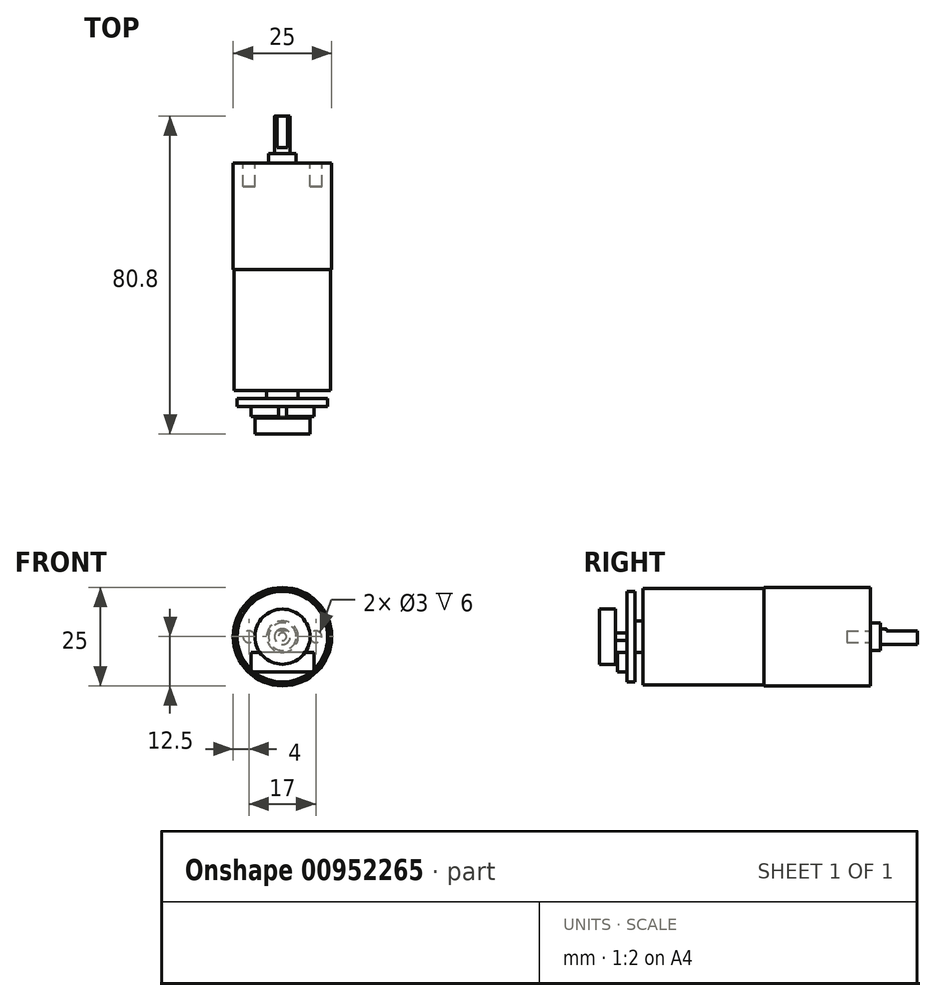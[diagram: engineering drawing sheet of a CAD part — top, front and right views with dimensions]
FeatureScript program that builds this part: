
annotation { "Feature Type Name" : "Feature", "Feature Type Description" : "" }
export const myFeature = defineFeature(function(context is Context, id is Id, definition is map)
    precondition{}
    {
        {
            var Q0;
            Q0=qCreatedBy(makeId("Front.planeOp"),FACE);
            var sketch = newSketch(context, id + "F0", { "sketchPlane" : qUnion([Q0])});
            skCircle(sketch, "E0", {"center": v(0, 0) * mm, "radius": 12.5 * mm});
            skSolve(sketch);
        }
        {
            var Q0;
            Q0 = qSketchRegion(id + "F0", true);
            extrude(context, id + "F1", {"entities" : qUnion([Q0]), "depth" : 27 * mm, "offsetDistance" : 25 * mm});
        }
        {
            var Q0;
            Q0=makeQuery(id+"F1.opExtrude","CAP_FACE",FACE,{"disambiguationData":[OSD([sQuery(id+"F0.wireOp",EDGE,"E0")])],"isStart":false});
            var sketch = newSketch(context, id + "F2", { "sketchPlane" : qUnion([Q0])});
            skCircle(sketch, "E1", {"center": v(0, 0) * mm, "radius": 12.25 * mm});
            skSolve(sketch);
        }
        {
            var Q0;
            Q0 = qSketchRegion(id + "F2", true);
            extrude(context, id + "F3", {"entities" : qUnion([Q0]), "operationType" : NewBodyOperationType.ADD, "depth" : 30.8 * mm, "offsetDistance" : 25 * mm});
        }
        {
            var Q0;
            Q0=makeQuery(id+"F1.opExtrude","CAP_FACE",FACE,{"disambiguationData":[OSD([sQuery(id+"F0.wireOp",EDGE,"E0")])],"isStart":true});
            var sketch = newSketch(context, id + "F4", { "sketchPlane" : qUnion([Q0])});
            skCircle(sketch, "E2", {"center": v(0, 0) * mm, "radius": 3.5 * mm});
            skSolve(sketch);
        }
        {
            var Q0;
            Q0 = qSketchRegion(id + "F4", true);
            extrude(context, id + "F5", {"entities" : qUnion([Q0]), "operationType" : NewBodyOperationType.ADD, "depth" : 2.5 * mm, "offsetDistance" : 25 * mm});
        }
        {
            var Q0;
            Q0=makeQuery(id+"F5.opExtrude","CAP_FACE",FACE,{"disambiguationData":[OSD([sQuery(id+"F4.wireOp",EDGE,"E2")])],"isStart":false});
            var sketch = newSketch(context, id + "F6", { "sketchPlane" : qUnion([Q0])});
            skCircle(sketch, "E3", {"center": v(0, 0) * mm, "radius": 2 * mm});
            skSolve(sketch);
        }
        {
            var Q0;
            Q0 = qSketchRegion(id + "F6", true);
            extrude(context, id + "F7", {"entities" : qUnion([Q0]), "operationType" : NewBodyOperationType.ADD, "depth" : 9.5 * mm, "offsetDistance" : 25 * mm});
        }
        {
            var Q0;
            Q0=makeQuery(id+"F7.opExtrude","CAP_FACE",FACE,{"disambiguationData":[OSD([sQuery(id+"F6.wireOp",EDGE,"E3")])],"isStart":false});
            var sketch = newSketch(context, id + "F8", { "sketchPlane" : qUnion([Q0])});
            skLineSegment(sketch, "E4", {"start": v(-1.32, 1.5) * mm, "end": v(1.32, 1.5) * mm});
            skArc(sketch, "E5", {"start": v(-1.32, 1.5) * mm, "mid": v(0, 2) * mm, "end": v(1.32, 1.5) * mm});
            skSolve(sketch);
        }
        {
            var Q0;
            Q0 = qSketchRegion(id + "F8", true);
            extrude(context, id + "F9", {"entities" : qUnion([Q0]), "operationType" : NewBodyOperationType.REMOVE, "oppositeDirection" : true, "depth" : 8 * mm, "offsetDistance" : 25 * mm});
        }
        {
            var Q0;
            Q0=makeQuery(id+"F1.opExtrude","CAP_FACE",FACE,{"disambiguationData":[OSD([sQuery(id+"F0.wireOp",EDGE,"E0")])],"isStart":true});
            var sketch = newSketch(context, id + "F10", { "sketchPlane" : qUnion([Q0])});
            skCircle(sketch, "E6", {"center": v(8.5, 0) * mm, "radius": 1.5 * mm});
            skCircle(sketch, "E7.MirrorC", {"center": v(-8.5, 0) * mm, "radius": 1.5 * mm});
            skSolve(sketch);
        }
        {
            var Q0;
            Q0 = qSketchRegion(id + "F10", true);
            extrude(context, id + "F11", {"entities" : qUnion([Q0]), "operationType" : NewBodyOperationType.REMOVE, "oppositeDirection" : true, "depth" : 6 * mm, "offsetDistance" : 25 * mm});
        }
        {
            var Q0;
            Q0=makeQuery(id+"F3.opExtrude","CAP_FACE",FACE,{"disambiguationData":[OSD([sQuery(id+"F2.wireOp",EDGE,"E1")])],"isStart":false});
            var sketch = newSketch(context, id + "F12", { "sketchPlane" : qUnion([Q0])});
            skCircle(sketch, "E8", {"center": v(0, 0) * mm, "radius": 4 * mm});
            skSolve(sketch);
        }
        {
            var Q0;
            Q0 = qSketchRegion(id + "F12", true);
            extrude(context, id + "F13", {"entities" : qUnion([Q0]), "operationType" : NewBodyOperationType.ADD, "depth" : 2 * mm, "offsetDistance" : 25 * mm});
        }
        {
            var Q0;
            Q0=makeQuery(id+"F13.opExtrude","CAP_FACE",FACE,{"disambiguationData":[OSD([sQuery(id+"F12.wireOp",EDGE,"E8")])],"isStart":false});
            var sketch = newSketch(context, id + "F14", { "sketchPlane" : qUnion([Q0])});
            skCircle(sketch, "E9", {"center": v(0, 0) * mm, "radius": 11.5 * mm});
            skSolve(sketch);
        }
        {
            var Q0;
            Q0 = qSketchRegion(id + "F14", true);
            extrude(context, id + "F15", {"entities" : qUnion([Q0]), "operationType" : NewBodyOperationType.ADD, "depth" : 2 * mm, "offsetDistance" : 25 * mm});
        }
        {
            var Q0;
            Q0=makeQuery(id+"F15.opExtrude","CAP_FACE",FACE,{"disambiguationData":[OSD([sQuery(id+"F14.wireOp",EDGE,"E9")])],"isStart":false});
            var sketch = newSketch(context, id + "F16", { "sketchPlane" : qUnion([Q0])});
            skCircle(sketch, "E10", {"center": v(0, 0) * mm, "radius": 1 * mm});
            skSolve(sketch);
        }
        {
            var Q0;
            Q0 = qSketchRegion(id + "F16", true);
            extrude(context, id + "F17", {"entities" : qUnion([Q0]), "operationType" : NewBodyOperationType.ADD, "depth" : (3.5 - 0.5) * mm, "offsetDistance" : 25 * mm});
        }
        {
            var Q0;
            Q0=makeQuery(id+"F17.opExtrude","CAP_FACE",FACE,{"disambiguationData":[OSD([sQuery(id+"F16.wireOp",EDGE,"E10")])],"isStart":false});
            var sketch = newSketch(context, id + "F18", { "sketchPlane" : qUnion([Q0])});
            skCircle(sketch, "E11", {"center": v(0, 0) * mm, "radius": 7 * mm});
            skSolve(sketch);
        }
        {
            var Q0;
            Q0 = qSketchRegion(id + "F18", true);
            extrude(context, id + "F19", {"entities" : qUnion([Q0]), "operationType" : NewBodyOperationType.ADD, "depth" : 4 * mm, "offsetDistance" : 25 * mm});
        }
        {
            var Q0;
            Q0=makeQuery(id+"F15.opExtrude","CAP_FACE",FACE,{"disambiguationData":[OSD([sQuery(id+"F14.wireOp",EDGE,"E9")])],"isStart":false});
            var sketch = newSketch(context, id + "F20", { "sketchPlane" : qUnion([Q0])});
            skLineSegment(sketch, "E12.bottom", {"start": v(8, -4) * mm, "end": v(-8, -4) * mm});
            skLineSegment(sketch, "E12.top", {"start": v(8, -9) * mm, "end": v(-8, -9) * mm});
            skLineSegment(sketch, "E12.left", {"start": v(8, -4) * mm, "end": v(8, -9) * mm});
            skLineSegment(sketch, "E12.right", {"start": v(-8, -4) * mm, "end": v(-8, -9) * mm});
            skPoint(sketch, "E12.middle", {"position": v(0, -6.5) * mm});
            skSolve(sketch);
        }
        {
            var Q0;
            Q0 = qSketchRegion(id + "F20", true);
            extrude(context, id + "F21", {"entities" : qUnion([Q0]), "operationType" : NewBodyOperationType.ADD, "depth" : 2.5 * mm, "offsetDistance" : 25 * mm});
        }
    });
